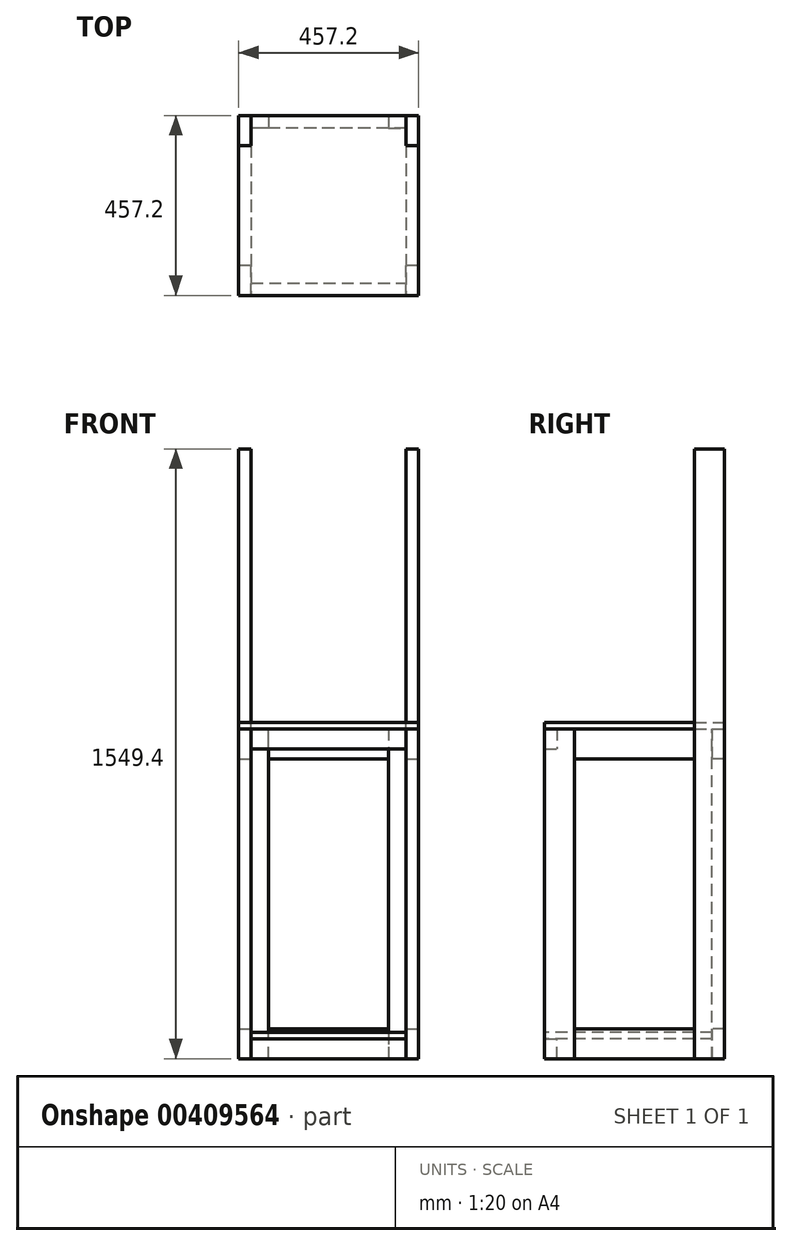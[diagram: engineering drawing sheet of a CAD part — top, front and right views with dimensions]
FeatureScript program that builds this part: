
annotation { "Feature Type Name" : "Feature", "Feature Type Description" : "" }
export const myFeature = defineFeature(function(context is Context, id is Id, definition is map)
    precondition{}
    {
        {
            var Q0;
            Q0=qCreatedBy(makeId("Top.planeOp"),FACE);
            cPlane(context, id + "F0", {"entities" : qUnion([Q0]), "cplaneType" : CPlaneType.OFFSET, "offset" : 711.2 * mm, "width" : 152.4 * mm, "height" : 152.4 * mm});
        }
        {
            var Q0;
            Q0=qCreatedBy(makeId("Top.planeOp"),FACE);
            cPlane(context, id + "F1", {"entities" : qUnion([Q0]), "cplaneType" : CPlaneType.OFFSET, "offset" : 838.2 * mm, "oppositeDirection" : true, "width" : 152.4 * mm, "height" : 152.4 * mm});
        }
        {
            var Q0;
            Q0=qCreatedBy(id+"F0.planeOp",FACE);
            var sketch = newSketch(context, id + "F2", { "sketchPlane" : qUnion([Q0])});
            skLineSegment(sketch, "E0.bottom", {"start": v(-457.2, 457.2) * mm, "end": v(-425.45, 457.2) * mm});
            skLineSegment(sketch, "E0.top", {"start": v(-457.2, 381) * mm, "end": v(-425.45, 381) * mm});
            skLineSegment(sketch, "E0.left", {"start": v(-457.2, 457.2) * mm, "end": v(-457.2, 381) * mm});
            skLineSegment(sketch, "E0.right", {"start": v(-425.45, 457.2) * mm, "end": v(-425.45, 381) * mm});
            skLineSegment(sketch, "E1.bottom", {"start": v(-31.75, 457.2) * mm, "end": v(0, 457.2) * mm});
            skLineSegment(sketch, "E1.top", {"start": v(-31.75, 381) * mm, "end": v(0, 381) * mm});
            skLineSegment(sketch, "E1.left", {"start": v(-31.75, 457.2) * mm, "end": v(-31.75, 381) * mm});
            skLineSegment(sketch, "E1.right", {"start": v(0, 457.2) * mm, "end": v(0, 381) * mm});
            skSolve(sketch);
        }
        {
            var Q0;
            Q0=qCreatedBy(makeId("Top.planeOp"),FACE);
            var sketch = newSketch(context, id + "F3", { "sketchPlane" : qUnion([Q0])});
            skLineSegment(sketch, "E2.bottom", {"start": v(-457.2, 76.2) * mm, "end": v(-425.45, 76.2) * mm});
            skLineSegment(sketch, "E2.top", {"start": v(-457.2, 0) * mm, "end": v(-425.45, 0) * mm});
            skLineSegment(sketch, "E2.left", {"start": v(-425.45, 76.2) * mm, "end": v(-425.45, 0) * mm});
            skLineSegment(sketch, "E2.right", {"start": v(-457.2, 76.2) * mm, "end": v(-457.2, 0) * mm});
            skLineSegment(sketch, "E3.bottom", {"start": v(-31.75, 76.2) * mm, "end": v(0, 76.2) * mm});
            skLineSegment(sketch, "E3.top", {"start": v(-31.75, 0) * mm, "end": v(0, 0) * mm});
            skLineSegment(sketch, "E3.left", {"start": v(-31.75, 76.2) * mm, "end": v(-31.75, 0) * mm});
            skLineSegment(sketch, "E3.right", {"start": v(0, 76.2) * mm, "end": v(0, 0) * mm});
            skSolve(sketch);
        }
        {
            var Q0;
            Q0 = qSketchRegion(id + "F2", true);
            var Q1;
            Q1 = qSketchRegion(id + "F3", true);
            var Q2;
            Q2=qCreatedBy(id+"F1.planeOp",FACE);
            extrude(context, id + "F4", {"entities" : qUnion([Q0, Q1]), "endBound" : BoundingType.UP_TO_SURFACE, "oppositeDirection" : true, "endBoundEntityFace" : qUnion([Q2]), "depth" : 25.4 * mm});
        }
        {
            var Q0;
            Q0=makeQuery(id+"F4.opExtrude","SWEPT_FACE",FACE,{"disambiguationData":[OSD([sQuery(id+"F3.wireOp",EDGE,"E3.bottom")])]});
            var sketch = newSketch(context, id + "F5", { "sketchPlane" : qUnion([Q0])});
            skLineSegment(sketch, "E4.bottom", {"start": v(0, 0) * mm, "end": v(31.75, 0) * mm});
            skLineSegment(sketch, "E4.top", {"start": v(0, -76.2) * mm, "end": v(31.75, -76.2) * mm});
            skLineSegment(sketch, "E4.left", {"start": v(0, 0) * mm, "end": v(0, -76.2) * mm});
            skLineSegment(sketch, "E4.right", {"start": v(31.75, 0) * mm, "end": v(31.75, -76.2) * mm});
            skLineSegment(sketch, "E5.bottom", {"start": v(425.45, 0) * mm, "end": v(457.2, 0) * mm});
            skLineSegment(sketch, "E5.top", {"start": v(425.45, -76.2) * mm, "end": v(457.2, -76.2) * mm});
            skLineSegment(sketch, "E5.left", {"start": v(425.45, 0) * mm, "end": v(425.45, -76.2) * mm});
            skLineSegment(sketch, "E5.right", {"start": v(457.2, 0) * mm, "end": v(457.2, -76.2) * mm});
            skLineSegment(sketch, "E6.bottom", {"start": v(0, -838.2) * mm, "end": v(31.75, -838.2) * mm});
            skLineSegment(sketch, "E6.top", {"start": v(0, -762) * mm, "end": v(31.75, -762) * mm});
            skLineSegment(sketch, "E6.left", {"start": v(0, -838.2) * mm, "end": v(0, -762) * mm});
            skLineSegment(sketch, "E6.right", {"start": v(31.75, -838.2) * mm, "end": v(31.75, -762) * mm});
            skLineSegment(sketch, "E7.bottom", {"start": v(425.45, -838.2) * mm, "end": v(457.2, -838.2) * mm});
            skLineSegment(sketch, "E7.top", {"start": v(425.45, -762) * mm, "end": v(457.2, -762) * mm});
            skLineSegment(sketch, "E7.left", {"start": v(425.45, -838.2) * mm, "end": v(425.45, -762) * mm});
            skLineSegment(sketch, "E7.right", {"start": v(457.2, -838.2) * mm, "end": v(457.2, -762) * mm});
            skSolve(sketch);
        }
        {
            var Q0;
            Q0 = qSketchRegion(id + "F5", true);
            var Q1;
            Q1=makeQuery(id+"F4.opExtrude","SWEPT_FACE",FACE,{"disambiguationData":[OSD([sQuery(id+"F2.wireOp",EDGE,"E0.top")])]});
            extrude(context, id + "F6", {"entities" : qUnion([Q0]), "endBound" : BoundingType.UP_TO_SURFACE, "endBoundEntityFace" : qUnion([Q1]), "depth" : 25.4 * mm});
        }
        {
            var Q0;
            Q0=makeQuery(id+"F4.opExtrude","SWEPT_FACE",FACE,{"disambiguationData":[OSD([sQuery(id+"F3.wireOp",EDGE,"E3.left")])]});
            var sketch = newSketch(context, id + "F7", { "sketchPlane" : qUnion([Q0])});
            skLineSegment(sketch, "E8.bottom", {"start": v(0, 0) * mm, "end": v(-31.75, 0) * mm});
            skLineSegment(sketch, "E8.top", {"start": v(0, -50.8) * mm, "end": v(-31.75, -50.8) * mm});
            skLineSegment(sketch, "E8.left", {"start": v(0, 0) * mm, "end": v(0, -50.8) * mm});
            skLineSegment(sketch, "E8.right", {"start": v(-31.75, 0) * mm, "end": v(-31.75, -50.8) * mm});
            skLineSegment(sketch, "E9.bottom", {"start": v(0, -838.2) * mm, "end": v(-31.75, -838.2) * mm});
            skLineSegment(sketch, "E9.top", {"start": v(0, -787.4) * mm, "end": v(-31.75, -787.4) * mm});
            skLineSegment(sketch, "E9.left", {"start": v(0, -838.2) * mm, "end": v(0, -787.4) * mm});
            skLineSegment(sketch, "E9.right", {"start": v(-31.75, -838.2) * mm, "end": v(-31.75, -787.4) * mm});
            skSolve(sketch);
        }
        {
            var Q0;
            Q0 = qSketchRegion(id + "F7", true);
            var Q1;
            Q1=makeQuery(id+"F4.opExtrude","SWEPT_FACE",FACE,{"disambiguationData":[OSD([sQuery(id+"F3.wireOp",EDGE,"E2.left")])]});
            extrude(context, id + "F8", {"entities" : qUnion([Q0]), "endBound" : BoundingType.UP_TO_SURFACE, "endBoundEntityFace" : qUnion([Q1]), "depth" : 25.4 * mm});
        }
        {
            var Q0;
            Q0=qCreatedBy(makeId("Top.planeOp"),FACE);
            var sketch = newSketch(context, id + "F9", { "sketchPlane" : qUnion([Q0])});
            skLineSegment(sketch, "E10.bottom", {"start": v(-425.45, 457.2) * mm, "end": v(-381, 457.2) * mm});
            skLineSegment(sketch, "E10.top", {"start": v(-425.45, 425.45) * mm, "end": v(-381, 425.45) * mm});
            skLineSegment(sketch, "E10.left", {"start": v(-425.45, 457.2) * mm, "end": v(-425.45, 425.45) * mm});
            skLineSegment(sketch, "E10.right", {"start": v(-381, 457.2) * mm, "end": v(-381, 425.45) * mm});
            skLineSegment(sketch, "E11.bottom", {"start": v(-31.75, 457.2) * mm, "end": v(-76.2, 457.2) * mm});
            skLineSegment(sketch, "E11.top", {"start": v(-31.75, 425.45) * mm, "end": v(-76.2, 425.45) * mm});
            skLineSegment(sketch, "E11.left", {"start": v(-31.75, 457.2) * mm, "end": v(-31.75, 425.45) * mm});
            skLineSegment(sketch, "E11.right", {"start": v(-76.2, 457.2) * mm, "end": v(-76.2, 425.45) * mm});
            skSolve(sketch);
        }
        {
            var Q0;
            Q0 = qSketchRegion(id + "F9", true);
            var Q1;
            {Q1=qUnion([makeQuery(id+"F4.opExtrude","CAP_FACE",FACE,{"disambiguationData":[OSD([sQuery(id+"F2.wireOp",EDGE,"E0.bottom"),sQuery(id+"F2.wireOp",EDGE,"E0.top"),sQuery(id+"F2.wireOp",EDGE,"E0.left"),sQuery(id+"F2.wireOp",EDGE,"E0.right")])],"isStart":false}),makeQuery(id+"F4.opExtrude","CAP_FACE",FACE,{"disambiguationData":[OSD([sQuery(id+"F2.wireOp",EDGE,"E1.bottom"),sQuery(id+"F2.wireOp",EDGE,"E1.top"),sQuery(id+"F2.wireOp",EDGE,"E1.left"),sQuery(id+"F2.wireOp",EDGE,"E1.right")])],"isStart":false}),makeQuery(id+"F4.opExtrude","CAP_FACE",FACE,{"disambiguationData":[OSD([sQuery(id+"F3.wireOp",EDGE,"E2.bottom"),sQuery(id+"F3.wireOp",EDGE,"E2.top"),sQuery(id+"F3.wireOp",EDGE,"E2.left"),sQuery(id+"F3.wireOp",EDGE,"E2.right")])],"isStart":false}),makeQuery(id+"F4.opExtrude","CAP_FACE",FACE,{"disambiguationData":[OSD([sQuery(id+"F3.wireOp",EDGE,"E3.bottom"),sQuery(id+"F3.wireOp",EDGE,"E3.top"),sQuery(id+"F3.wireOp",EDGE,"E3.left"),sQuery(id+"F3.wireOp",EDGE,"E3.right")])],"isStart":false})]);}
            extrude(context, id + "F10", {"entities" : qUnion([Q0]), "endBound" : BoundingType.UP_TO_SURFACE, "oppositeDirection" : true, "endBoundEntityFace" : qUnion([Q1]), "depth" : 25.4 * mm});
        }
        {
            var Q0;
            Q0=makeQuery(id+"F10.opExtrude","SWEPT_FACE",FACE,{"disambiguationData":[OSD([sQuery(id+"F9.wireOp",EDGE,"E10.right")])]});
            var sketch = newSketch(context, id + "F11", { "sketchPlane" : qUnion([Q0])});
            skLineSegment(sketch, "E12.bottom", {"start": v(425.45, 0) * mm, "end": v(457.2, 0) * mm});
            skLineSegment(sketch, "E12.top", {"start": v(425.45, -76.2) * mm, "end": v(457.2, -76.2) * mm});
            skLineSegment(sketch, "E12.left", {"start": v(425.45, 0) * mm, "end": v(425.45, -76.2) * mm});
            skLineSegment(sketch, "E12.right", {"start": v(457.2, 0) * mm, "end": v(457.2, -76.2) * mm});
            skLineSegment(sketch, "E13.bottom", {"start": v(425.45, -838.2) * mm, "end": v(457.2, -838.2) * mm});
            skLineSegment(sketch, "E13.top", {"start": v(425.45, -762) * mm, "end": v(457.2, -762) * mm});
            skLineSegment(sketch, "E13.left", {"start": v(425.45, -838.2) * mm, "end": v(425.45, -762) * mm});
            skLineSegment(sketch, "E13.right", {"start": v(457.2, -838.2) * mm, "end": v(457.2, -762) * mm});
            skSolve(sketch);
        }
        {
            var Q0;
            Q0 = qSketchRegion(id + "F11", true);
            var Q1;
            Q1=makeQuery(id+"F10.opExtrude","SWEPT_FACE",FACE,{"disambiguationData":[OSD([sQuery(id+"F9.wireOp",EDGE,"E11.right")])]});
            extrude(context, id + "F12", {"entities" : qUnion([Q0]), "endBound" : BoundingType.UP_TO_SURFACE, "endBoundEntityFace" : qUnion([Q1]), "depth" : 25.4 * mm});
        }
        {
            var Q0;
            Q0=makeQuery(id+"F8.opExtrude","SWEPT_FACE",FACE,{"disambiguationData":[OSD([sQuery(id+"F7.wireOp",EDGE,"E8.left")])]});
            var sketch = newSketch(context, id + "F13", { "sketchPlane" : qUnion([Q0])});
            skLineSegment(sketch, "E14.bottom", {"start": v(-457.2, 0) * mm, "end": v(0, 0) * mm});
            skLineSegment(sketch, "E14.top", {"start": v(-457.2, 15.88) * mm, "end": v(0, 15.88) * mm});
            skLineSegment(sketch, "E14.left", {"start": v(-457.2, 0) * mm, "end": v(-457.2, 15.88) * mm});
            skLineSegment(sketch, "E14.right", {"start": v(0, 0) * mm, "end": v(0, 15.88) * mm});
            skSolve(sketch);
        }
        {
            var Q0;
            Q0 = qSketchRegion(id + "F13", true);
            var Q1;
            {Q1=qUnion([makeQuery(id+"F10.opExtrude","SWEPT_FACE",FACE,{"disambiguationData":[OSD([sQuery(id+"F9.wireOp",EDGE,"E10.bottom")])]}),makeQuery(id+"F12.opExtrude","SWEPT_FACE",FACE,{"disambiguationData":[OSD([sQuery(id+"F11.wireOp",EDGE,"E12.right")])]}),makeQuery(id+"F12.opExtrude","SWEPT_FACE",FACE,{"disambiguationData":[OSD([sQuery(id+"F11.wireOp",EDGE,"E13.right")])]})]);}
            extrude(context, id + "F14", {"entities" : qUnion([Q0]), "endBound" : BoundingType.UP_TO_SURFACE, "oppositeDirection" : true, "endBoundEntityFace" : qUnion([Q1]), "depth" : 25.4 * mm});
        }
        {
            var Q0;
            Q0=makeQuery(id+"F4.opExtrude","SWEPT_BODY",BODY,{"disambiguationData":[OSD([sQuery(id+"F2.wireOp",EDGE,"E0.bottom"),sQuery(id+"F2.wireOp",EDGE,"E0.top"),sQuery(id+"F2.wireOp",EDGE,"E0.left"),sQuery(id+"F2.wireOp",EDGE,"E0.right")])]});
            var Q1;
            Q1=makeQuery(id+"F4.opExtrude","SWEPT_BODY",BODY,{"disambiguationData":[OSD([sQuery(id+"F2.wireOp",EDGE,"E1.bottom"),sQuery(id+"F2.wireOp",EDGE,"E1.top"),sQuery(id+"F2.wireOp",EDGE,"E1.left"),sQuery(id+"F2.wireOp",EDGE,"E1.right")])]});
            var Q2;
            Q2=makeQuery(id+"F14.opExtrude","SWEPT_BODY",BODY,{"disambiguationData":[OSD([sQuery(id+"F13.wireOp",EDGE,"E14.bottom"),sQuery(id+"F13.wireOp",EDGE,"E14.top"),sQuery(id+"F13.wireOp",EDGE,"E14.left"),sQuery(id+"F13.wireOp",EDGE,"E14.right")])]});
            booleanBodies(context, id + "F15", {"operationType" : BooleanOperationType.SUBTRACTION, "tools" : qUnion([Q0, Q1]), "targets" : qUnion([Q2]), "keepTools" : true});
        }
        {
            var Q0;
            Q0=makeQuery(id+"F8.opExtrude","SWEPT_FACE",FACE,{"disambiguationData":[OSD([sQuery(id+"F7.wireOp",EDGE,"E9.left")])]});
            var sketch = newSketch(context, id + "F16", { "sketchPlane" : qUnion([Q0])});
            skLineSegment(sketch, "E15.bottom", {"start": v(-425.45, -787.4) * mm, "end": v(-31.75, -787.4) * mm});
            skLineSegment(sketch, "E15.top", {"start": v(-425.45, -771.53) * mm, "end": v(-31.75, -771.53) * mm});
            skLineSegment(sketch, "E15.left", {"start": v(-425.45, -787.4) * mm, "end": v(-425.45, -771.53) * mm});
            skLineSegment(sketch, "E15.right", {"start": v(-31.75, -787.4) * mm, "end": v(-31.75, -771.53) * mm});
            skSolve(sketch);
        }
        {
            var Q0;
            Q0 = qSketchRegion(id + "F16", true);
            var Q1;
            {Q1=qUnion([makeQuery(id+"F10.opExtrude","SWEPT_FACE",FACE,{"disambiguationData":[OSD([sQuery(id+"F9.wireOp",EDGE,"E10.top")])]}),makeQuery(id+"F12.opExtrude","SWEPT_FACE",FACE,{"disambiguationData":[OSD([sQuery(id+"F11.wireOp",EDGE,"E12.left")])]}),makeQuery(id+"F12.opExtrude","SWEPT_FACE",FACE,{"disambiguationData":[OSD([sQuery(id+"F11.wireOp",EDGE,"E13.left")])]})]);}
            extrude(context, id + "F17", {"entities" : qUnion([Q0]), "endBound" : BoundingType.UP_TO_SURFACE, "oppositeDirection" : true, "endBoundEntityFace" : qUnion([Q1]), "depth" : 25.4 * mm});
        }
    });
